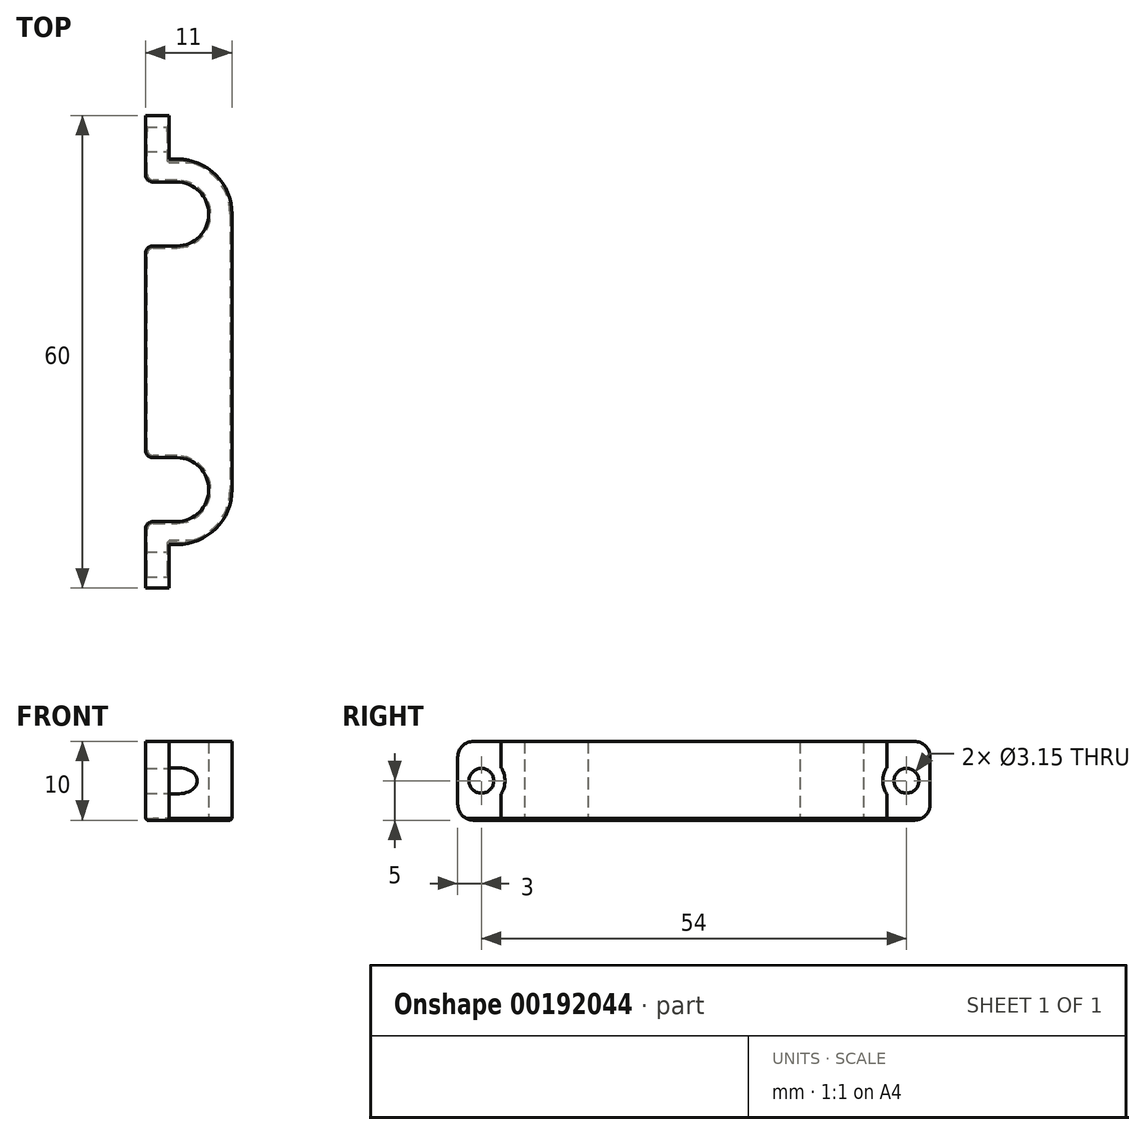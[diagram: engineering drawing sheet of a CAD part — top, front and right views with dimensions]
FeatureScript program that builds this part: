
annotation { "Feature Type Name" : "Feature", "Feature Type Description" : "" }
export const myFeature = defineFeature(function(context is Context, id is Id, definition is map)
    precondition{}
    {
        {
            var Q0;
            Q0=qCreatedBy(makeId("Top.planeOp"),FACE);
            var sketch = newSketch(context, id + "F0", { "sketchPlane" : qUnion([Q0])});
            skCircle(sketch, "E0", {"center": v(0, 17.5) * mm, "radius": 4 * mm, "construction": true});
            skArc(sketch, "E1", {"start": v(0, 21.55) * mm, "mid": v(4.05, 17.5) * mm, "end": v(0, 13.45) * mm});
            skLineSegment(sketch, "E2", {"start": v(0, 13.45) * mm, "end": v(-4, 13.45) * mm});
            skLineSegment(sketch, "E3", {"start": v(-4, 13.45) * mm, "end": v(-4, 0) * mm});
            skLineSegment(sketch, "E4", {"start": v(0, 21.55) * mm, "end": v(-4, 21.55) * mm});
            skLineSegment(sketch, "E5", {"start": v(-4, 21.55) * mm, "end": v(-4, 30) * mm});
            skLineSegment(sketch, "E6", {"start": v(-4, 30) * mm, "end": v(-1, 30) * mm});
            skLineSegment(sketch, "E7", {"start": v(-1, 30) * mm, "end": v(-1, 24.5) * mm});
            skLineSegment(sketch, "E8", {"start": v(-1, 24.5) * mm, "end": v(0, 24.5) * mm});
            skArc(sketch, "E9", {"start": v(0, 24.5) * mm, "mid": v(4.95, 22.45) * mm, "end": v(7, 17.5) * mm});
            skLineSegment(sketch, "E10", {"start": v(7, 17.5) * mm, "end": v(7, 0) * mm});
            skLineSegment(sketch, "E11.MirrorCS", {"start": v(-4, -13.45) * mm, "end": v(-4, 0) * mm});
            skLineSegment(sketch, "E12.MirrorCS", {"start": v(7, -17.5) * mm, "end": v(7, 0) * mm});
            skLineSegment(sketch, "E13.MirrorCS", {"start": v(0, -13.45) * mm, "end": v(-4, -13.45) * mm});
            skArc(sketch, "E14.MirrorCS", {"start": v(0, -21.55) * mm, "mid": v(4.05, -17.5) * mm, "end": v(0, -13.45) * mm});
            skArc(sketch, "E15.MirrorCS", {"start": v(0, -24.5) * mm, "mid": v(4.95, -22.45) * mm, "end": v(7, -17.5) * mm});
            skLineSegment(sketch, "E16.MirrorCS", {"start": v(0, -21.55) * mm, "end": v(-4, -21.55) * mm});
            skLineSegment(sketch, "E17.MirrorCS", {"start": v(-4, -21.55) * mm, "end": v(-4, -30) * mm});
            skCircle(sketch, "E18.MirrorC", {"center": v(0, -17.5) * mm, "radius": 4 * mm, "construction": true});
            skLineSegment(sketch, "E19.MirrorCS", {"start": v(-4, -30) * mm, "end": v(-1, -30) * mm});
            skLineSegment(sketch, "E20.MirrorCS", {"start": v(-1, -30) * mm, "end": v(-1, -24.5) * mm});
            skLineSegment(sketch, "E21.MirrorCS", {"start": v(-1, -24.5) * mm, "end": v(0, -24.5) * mm});
            skPoint(sketch, "E22", {"position": v(-4, 27) * mm});
            skPoint(sketch, "E23.MirrorP", {"position": v(-4, -27) * mm});
            skLineSegment(sketch, "E24", {"start": v(-4, 27) * mm, "end": v(-1, 27) * mm, "construction": true});
            skLineSegment(sketch, "E25.MirrorCS", {"start": v(-4, -27) * mm, "end": v(-1, -27) * mm, "construction": true});
            skSolve(sketch);
        }
        {
            var Q0;
            Q0=qSketchRegion(id+"F0",true);
            extrude(context, id + "F1", {"entities" : qUnion([Q0]), "depth" : 10 * mm, "symmetric" : true});
        }
        {
            var Q0;
            Q0=makeQuery(id+"F1.opExtrude","SWEPT_EDGE",EDGE,{"disambiguationData":[OSD([sQuery(id+"F0.wireOp",EDGE,"E4"),sQuery(id+"F0.wireOp",EDGE,"E5")])]});
            var Q1;
            Q1=makeQuery(id+"F1.opExtrude","SWEPT_EDGE",EDGE,{"disambiguationData":[OSD([sQuery(id+"F0.wireOp",EDGE,"E2"),sQuery(id+"F0.wireOp",EDGE,"E3")])]});
            var Q2;
            Q2=makeQuery(id+"F1.opExtrude","SWEPT_EDGE",EDGE,{"disambiguationData":[OSD([sQuery(id+"F0.wireOp",EDGE,"E16.MirrorCS"),sQuery(id+"F0.wireOp",EDGE,"E17.MirrorCS")])]});
            var Q3;
            Q3=makeQuery(id+"F1.opExtrude","SWEPT_EDGE",EDGE,{"disambiguationData":[OSD([sQuery(id+"F0.wireOp",EDGE,"E11.MirrorCS"),sQuery(id+"F0.wireOp",EDGE,"E13.MirrorCS")])]});
            fillet(context, id + "F2", {"entities" : qUnion([Q0, Q1, Q2, Q3]), "radius" : 1 * mm, "allowEdgeOverflow" : false});
        }
        {
            var Q0;
            Q0=makeQuery(id+"F1.opExtrude","SWEPT_FACE",FACE,{"disambiguationData":[OSD([sQuery(id+"F0.wireOp",EDGE,"E20.MirrorCS")])]});
            var sketch = newSketch(context, id + "F3", { "sketchPlane" : qUnion([Q0])});
            skPoint(sketch, "E26.0", {"position": v(-27, 0) * mm});
            skCircle(sketch, "E27", {"center": v(-27, 0) * mm, "radius": 1.57 * mm});
            skPoint(sketch, "E28.0", {"position": v(27, 0) * mm});
            skCircle(sketch, "E29", {"center": v(27, 0) * mm, "radius": 1.57 * mm});
            skCircle(sketch, "E30", {"center": v(27, 0) * mm, "radius": 3 * mm});
            skCircle(sketch, "E31", {"center": v(-27, 0) * mm, "radius": 3 * mm});
            skSolve(sketch);
        }
        {
            var Q0;
            Q0=makeQuery(id+"F3.imprint","IMPRINT",FACE,{"disambiguationData":[TD([[makeQuery(id+"F3.imprint","IMPRINT",EDGE,{"derivedFrom":sQuery(id+"F3.wireOp",EDGE,"E29")}),1.0]])]});
            var Q1;
            Q1=makeQuery(id+"F3.imprint","IMPRINT",FACE,{"disambiguationData":[TD([[makeQuery(id+"F3.imprint","IMPRINT",EDGE,{"derivedFrom":sQuery(id+"F3.wireOp",EDGE,"E27")}),1.0]])]});
            var Q2;
            Q2=makeQuery(id+"F1.opExtrude","SWEPT_FACE",FACE,{"disambiguationData":[OSD([sQuery(id+"F0.wireOp",EDGE,"E17.MirrorCS")])]});
            extrude(context, id + "F4", {"entities" : qUnion([Q0, Q1]), "operationType" : NewBodyOperationType.REMOVE, "endBound" : BoundingType.UP_TO_SURFACE, "oppositeDirection" : true, "endBoundEntityFace" : qUnion([Q2]), "depth" : 25 * mm});
        }
        {
            var Q0;
            {var subQ0=sQuery(id+"F3.wireOp",EDGE,"E31");var subQ1=makeQuery(id+"F1.opExtrude","SWEPT_EDGE",EDGE,{"disambiguationData":[OSD([sQuery(id+"F0.wireOp",EDGE,"E20.MirrorCS"),sQuery(id+"F0.wireOp",EDGE,"E21.MirrorCS")])]});var subQ2=makeQuery(id+"F3.imprint","INTERSECT",VERTEX,{"disambiguationData":[OD(0.0)],"derivedFrom":[subQ1,subQ0]});Q0=makeQuery(id+"F3.imprint","IMPRINT",FACE,{"disambiguationData":[TD([[makeQuery(id+"F3.imprint","IMPRINT",EDGE,{"disambiguationData":[TD([[subQ2,1.0]])],"derivedFrom":subQ0}),1.0]])]});}
            var Q1;
            Q1=makeQuery(id+"F3.imprint","IMPRINT",FACE,{"disambiguationData":[TD([[makeQuery(id+"F3.imprint","IMPRINT",EDGE,{"derivedFrom":sQuery(id+"F3.wireOp",EDGE,"E29")}),-1.0]])]});
            extrude(context, id + "F5", {"entities" : qUnion([Q0, Q1]), "operationType" : NewBodyOperationType.REMOVE, "endBound" : BoundingType.THROUGH_ALL, "depth" : 25 * mm});
        }
        {
            var Q0;
            Q0=makeQuery(id+"F1.opExtrude","CAP_EDGE",EDGE,{"disambiguationData":[OSD([sQuery(id+"F0.wireOp",EDGE,"E6")])],"isStart":true});
            var Q1;
            Q1=makeQuery(id+"F1.opExtrude","CAP_EDGE",EDGE,{"disambiguationData":[OSD([sQuery(id+"F0.wireOp",EDGE,"E6")])],"isStart":false});
            var Q2;
            Q2=makeQuery(id+"F1.opExtrude","CAP_EDGE",EDGE,{"disambiguationData":[OSD([sQuery(id+"F0.wireOp",EDGE,"E19.MirrorCS")])],"isStart":true});
            var Q3;
            Q3=makeQuery(id+"F1.opExtrude","CAP_EDGE",EDGE,{"disambiguationData":[OSD([sQuery(id+"F0.wireOp",EDGE,"E19.MirrorCS")])],"isStart":false});
            fillet(context, id + "F6", {"entities" : qUnion([Q0, Q1, Q2, Q3]), "radius" : 2 * mm, "allowEdgeOverflow" : false});
        }
        {
            var Q0;
            Q0=makeQuery(id+"F1.opExtrude","CAP_FACE",FACE,{"disambiguationData":[OSD([sQuery(id+"F0.wireOp",EDGE,"E1"),sQuery(id+"F0.wireOp",EDGE,"E2"),sQuery(id+"F0.wireOp",EDGE,"E3"),sQuery(id+"F0.wireOp",EDGE,"E4"),sQuery(id+"F0.wireOp",EDGE,"E5"),sQuery(id+"F0.wireOp",EDGE,"E6"),sQuery(id+"F0.wireOp",EDGE,"E7"),sQuery(id+"F0.wireOp",EDGE,"E8"),sQuery(id+"F0.wireOp",EDGE,"E9"),sQuery(id+"F0.wireOp",EDGE,"E10"),sQuery(id+"F0.wireOp",EDGE,"E11.MirrorCS"),sQuery(id+"F0.wireOp",EDGE,"E12.MirrorCS"),sQuery(id+"F0.wireOp",EDGE,"E13.MirrorCS"),sQuery(id+"F0.wireOp",EDGE,"E14.MirrorCS"),sQuery(id+"F0.wireOp",EDGE,"E15.MirrorCS"),sQuery(id+"F0.wireOp",EDGE,"E16.MirrorCS"),sQuery(id+"F0.wireOp",EDGE,"E17.MirrorCS"),sQuery(id+"F0.wireOp",EDGE,"E19.MirrorCS"),sQuery(id+"F0.wireOp",EDGE,"E20.MirrorCS"),sQuery(id+"F0.wireOp",EDGE,"E21.MirrorCS")])],"isStart":true});
            chamfer(context, id + "F7", {"entities" : qUnion([Q0]), "width" : 0.25 * mm});
        }
    });
